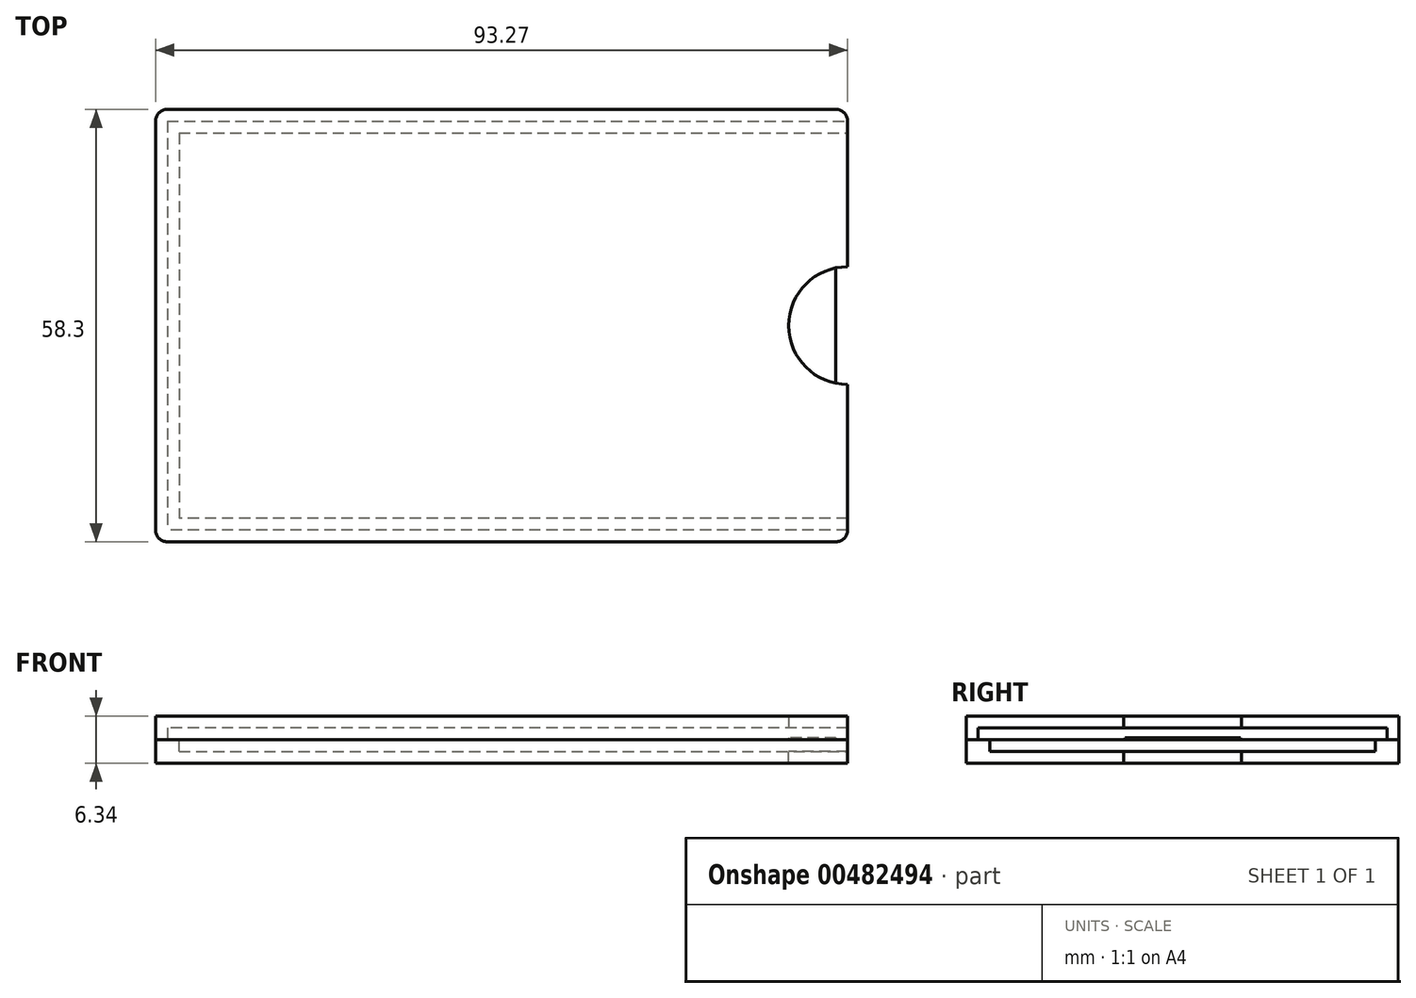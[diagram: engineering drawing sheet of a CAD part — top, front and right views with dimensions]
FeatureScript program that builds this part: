
annotation { "Feature Type Name" : "Feature", "Feature Type Description" : "" }
export const myFeature = defineFeature(function(context is Context, id is Id, definition is map)
    precondition{}
    {
        {
            var Q0;
            Q0=qCreatedBy(makeId("Top.planeOp"),FACE);
            var sketch = newSketch(context, id + "F0", { "sketchPlane" : qUnion([Q0])});
            skLineSegment(sketch, "E0.bottom", {"start": v(44.45, 25.4) * mm, "end": v(-44.45, 25.4) * mm});
            skLineSegment(sketch, "E0.top", {"start": v(44.45, -25.4) * mm, "end": v(-44.45, -25.4) * mm});
            skLineSegment(sketch, "E0.left", {"start": v(44.45, 25.4) * mm, "end": v(44.45, -25.4) * mm});
            skLineSegment(sketch, "E0.right", {"start": v(-44.45, 25.4) * mm, "end": v(-44.45, -25.4) * mm});
            skPoint(sketch, "E0.middle", {"position": v(0, 0) * mm});
            skSolve(sketch);
        }
        {
            var Q0;
            Q0=qCreatedBy(makeId("Top.planeOp"),FACE);
            var sketch = newSketch(context, id + "F1", { "sketchPlane" : qUnion([Q0])});
            skLineSegment(sketch, "E1", {"start": v(46.04, 25.97) * mm, "end": v(-44.05, 25.97) * mm});
            skLineSegment(sketch, "E2", {"start": v(-44.05, 25.97) * mm, "end": v(-44.05, -25.97) * mm});
            skLineSegment(sketch, "E3", {"start": v(-44.05, -25.97) * mm, "end": v(46.04, -25.97) * mm});
            skLineSegment(sketch, "E4", {"start": v(44.45, 29.15) * mm, "end": v(-45.64, 29.15) * mm});
            skLineSegment(sketch, "E5", {"start": v(-47.23, 27.56) * mm, "end": v(-47.23, -27.56) * mm});
            skLineSegment(sketch, "E6", {"start": v(-45.64, -29.15) * mm, "end": v(44.45, -29.15) * mm});
            skPoint(sketch, "E7.startSnap0", {"position": v(46.04, 0) * mm});
            skArc(sketch, "E8", {"start": v(46.04, -7.94) * mm, "mid": v(38.1, 0) * mm, "end": v(46.04, 7.94) * mm});
            skLineSegment(sketch, "E9", {"start": v(46.04, 27.56) * mm, "end": v(46.04, 7.94) * mm});
            skLineSegment(sketch, "E10", {"start": v(46.04, -7.94) * mm, "end": v(46.04, -27.56) * mm});
            skPoint(sketch, "E11", {"position": v(-44.05, 0) * mm});
            skPoint(sketch, "E12.visualSharp", {"position": v(-47.23, 29.15) * mm});
            skArc(sketch, "E12.filletArc", {"start": v(-45.64, 29.15) * mm, "mid": v(-46.76, 28.68) * mm, "end": v(-47.23, 27.56) * mm});
            skPoint(sketch, "E13.visualSharp", {"position": v(-47.23, -29.15) * mm});
            skArc(sketch, "E13.filletArc", {"start": v(-47.23, -27.56) * mm, "mid": v(-46.76, -28.68) * mm, "end": v(-45.64, -29.15) * mm});
            skPoint(sketch, "E14.visualSharp", {"position": v(46.04, -29.15) * mm});
            skArc(sketch, "E14.filletArc", {"start": v(44.45, -29.15) * mm, "mid": v(45.57, -28.68) * mm, "end": v(46.04, -27.56) * mm});
            skPoint(sketch, "E15.visualSharp", {"position": v(46.04, 29.15) * mm});
            skArc(sketch, "E15.filletArc", {"start": v(46.04, 27.56) * mm, "mid": v(45.57, 28.68) * mm, "end": v(44.45, 29.15) * mm});
            skLineSegment(sketch, "E16", {"start": v(46.04, -27.56) * mm, "end": v(-45.64, -27.56) * mm});
            skLineSegment(sketch, "E17", {"start": v(-45.64, 27.56) * mm, "end": v(-45.64, -27.56) * mm});
            skLineSegment(sketch, "E18", {"start": v(-45.64, 27.56) * mm, "end": v(46.04, 27.56) * mm});
            skLineSegment(sketch, "E19", {"start": v(46.04, 27.56) * mm, "end": v(49.21, 27.56) * mm});
            skLineSegment(sketch, "E20", {"start": v(49.21, 27.56) * mm, "end": v(49.21, -27.56) * mm});
            skLineSegment(sketch, "E21", {"start": v(49.21, -27.56) * mm, "end": v(46.04, -27.56) * mm});
            skLineSegment(sketch, "E22", {"start": v(46.04, 25.97) * mm, "end": v(49.21, 25.97) * mm});
            skLineSegment(sketch, "E23", {"start": v(46.04, -25.97) * mm, "end": v(49.21, -25.97) * mm});
            skSolve(sketch);
        }
        {
            var Q0;
            Q0=makeQuery(id+"F0.imprint","IMPRINT",FACE,{"disambiguationData":[TD([[makeQuery(id+"F0.imprint","IMPRINT",EDGE,{"derivedFrom":sQuery(id+"F0.wireOp",EDGE,"E0.bottom")}),1.0]])]});
            extrude(context, id + "F2", {"entities" : qUnion([Q0]), "depth" : 0.25 * mm});
        }
        {
            var Q0;
            {var subQ4=sQuery(id+"F1.wireOp",EDGE,"E1");Q0=makeQuery(id+"F1.imprint","IMPRINT",FACE,{"disambiguationData":[TD([[makeQuery(id+"F1.imprint","IMPRINT",EDGE,{"derivedFrom":subQ4}),-1.0]])]});}
            var Q1;
            {var subQ2=sQuery(id+"F1.wireOp",EDGE,"E1");Q1=makeQuery(id+"F1.imprint","IMPRINT",FACE,{"disambiguationData":[TD([[makeQuery(id+"F1.imprint","IMPRINT",EDGE,{"derivedFrom":subQ2}),1.0]])]});}
            var Q2;
            Q2=makeQuery(id+"F1.imprint","IMPRINT",FACE,{"disambiguationData":[TD([[makeQuery(id+"F1.imprint","IMPRINT",EDGE,{"derivedFrom":sQuery(id+"F1.wireOp",EDGE,"E4")}),1.0]])]});
            extrude(context, id + "F3", {"entities" : qUnion([Q0, Q1, Q2]), "oppositeDirection" : true, "depth" : 3.17 * mm});
        }
        {
            var Q0;
            {var subQ2=sQuery(id+"F1.wireOp",EDGE,"E1");Q0=makeQuery(id+"F1.imprint","IMPRINT",FACE,{"disambiguationData":[TD([[makeQuery(id+"F1.imprint","IMPRINT",EDGE,{"derivedFrom":subQ2}),1.0]])]});}
            extrude(context, id + "F4", {"entities" : qUnion([Q0]), "operationType" : NewBodyOperationType.REMOVE, "oppositeDirection" : true, "depth" : 1.59 * mm});
        }
        {
            var Q0;
            {var subQ1=sQuery(id+"F1.wireOp",EDGE,"E1");Q0=makeQuery(id+"F1.imprint","IMPRINT",FACE,{"disambiguationData":[TD([[makeQuery(id+"F1.imprint","IMPRINT",EDGE,{"derivedFrom":subQ1}),-1.0]])]});}
            extrude(context, id + "F5", {"entities" : qUnion([Q0]), "operationType" : NewBodyOperationType.ADD, "depth" : 1.59 * mm});
        }
        {
            var Q0;
            {var subQ2=sQuery(id+"F1.wireOp",EDGE,"E1");Q0=makeQuery(id+"F1.imprint","IMPRINT",FACE,{"disambiguationData":[TD([[makeQuery(id+"F1.imprint","IMPRINT",EDGE,{"derivedFrom":subQ2}),1.0]])]});}
            var Q1;
            {var subQ1=sQuery(id+"F1.wireOp",EDGE,"E1");Q1=makeQuery(id+"F1.imprint","IMPRINT",FACE,{"disambiguationData":[TD([[makeQuery(id+"F1.imprint","IMPRINT",EDGE,{"derivedFrom":subQ1}),-1.0]])]});}
            var Q2;
            Q2=makeQuery(id+"F1.imprint","IMPRINT",FACE,{"disambiguationData":[TD([[makeQuery(id+"F1.imprint","IMPRINT",EDGE,{"derivedFrom":sQuery(id+"F1.wireOp",EDGE,"E4")}),1.0]])]});
            extrude(context, id + "F6", {"entities" : qUnion([Q0, Q1, Q2]), "depth" : 3.17 * mm});
        }
        {
            var Q0;
            {var subQ2=sQuery(id+"F1.wireOp",EDGE,"E1");Q0=makeQuery(id+"F1.imprint","IMPRINT",FACE,{"disambiguationData":[TD([[makeQuery(id+"F1.imprint","IMPRINT",EDGE,{"derivedFrom":subQ2}),1.0]])]});}
            var Q1;
            {var subQ1=sQuery(id+"F1.wireOp",EDGE,"E1");Q1=makeQuery(id+"F1.imprint","IMPRINT",FACE,{"disambiguationData":[TD([[makeQuery(id+"F1.imprint","IMPRINT",EDGE,{"derivedFrom":subQ1}),-1.0]])]});}
            extrude(context, id + "F7", {"entities" : qUnion([Q0, Q1]), "operationType" : NewBodyOperationType.REMOVE, "depth" : 1.59 * mm});
        }
    });
